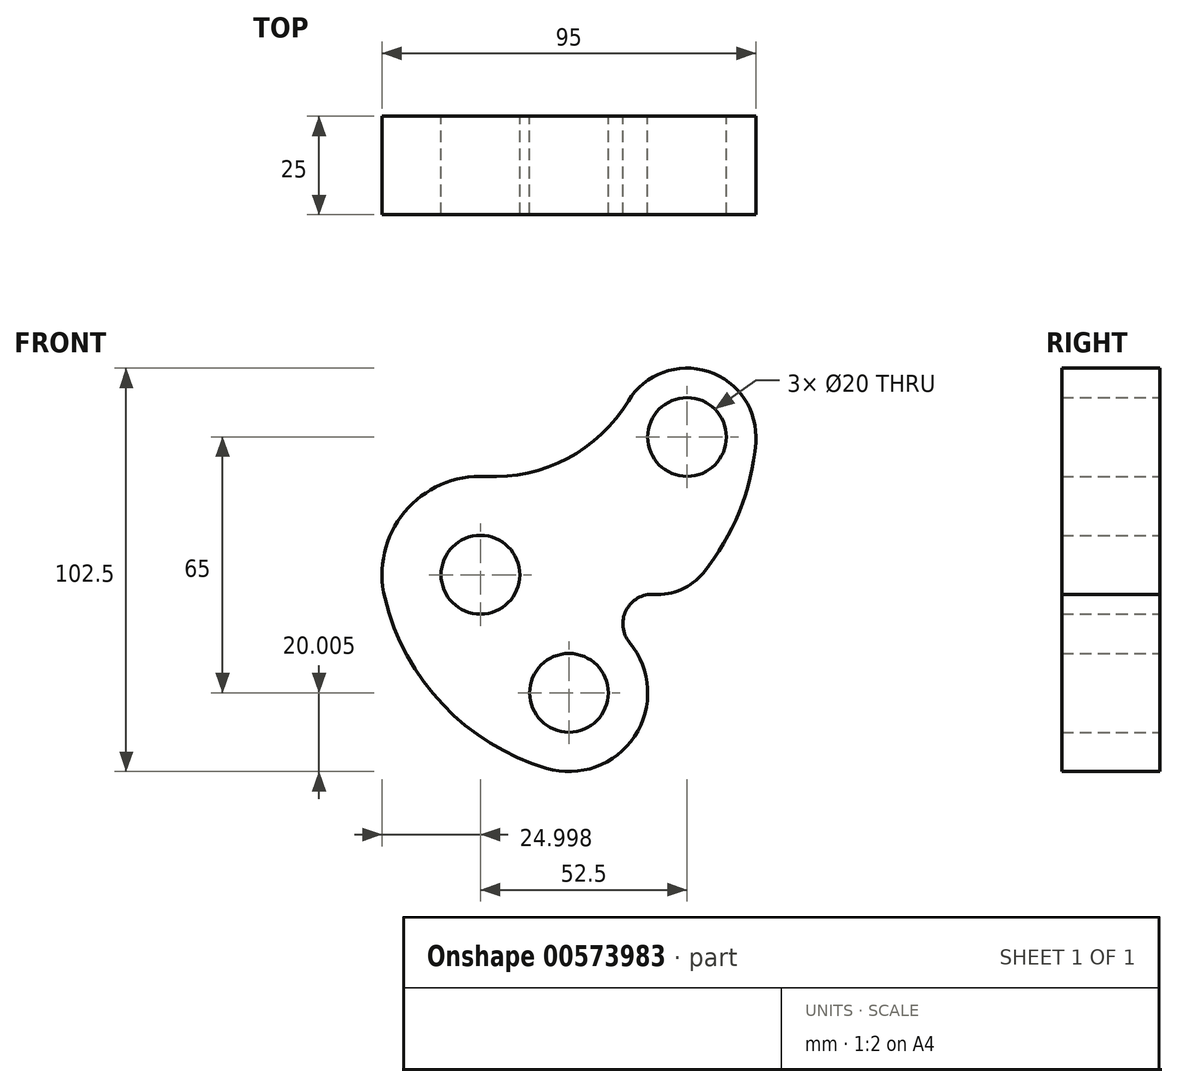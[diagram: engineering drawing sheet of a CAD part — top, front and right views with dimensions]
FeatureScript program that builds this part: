
annotation { "Feature Type Name" : "Feature", "Feature Type Description" : "" }
export const myFeature = defineFeature(function(context is Context, id is Id, definition is map)
    precondition{}
    {
        {
            var Q0;
            Q0=qCreatedBy(makeId("Front.planeOp"),FACE);
            var sketch = newSketch(context, id + "F0", { "sketchPlane" : qUnion([Q0])});
            skCircle(sketch, "E0", {"center": v(31.17, 52.24) * mm, "radius": 10 * mm});
            skCircle(sketch, "E1", {"center": v(-21.33, 17.24) * mm, "radius": 10 * mm});
            skCircle(sketch, "E2", {"center": v(1.17, -12.76) * mm, "radius": 10 * mm});
            skArc(sketch, "E3", {"start": v(-4.58, -31.91) * mm, "mid": v(17.84, -23.8) * mm, "end": v(16.57, 0) * mm});
            skArc(sketch, "E4", {"start": v(-20.03, 42.21) * mm, "mid": v(-40.59, 33.19) * mm, "end": v(-45.62, 11.3) * mm});
            skArc(sketch, "E5", {"start": v(48.6, 50.82) * mm, "mid": v(36.58, 68.89) * mm, "end": v(16.22, 61.35) * mm});
            skArc(sketch, "E6", {"start": v(-20.03, 42.21) * mm, "mid": v(0.73, 46.78) * mm, "end": v(16.22, 61.35) * mm});
            skArc(sketch, "E7", {"start": v(-45.62, 11.3) * mm, "mid": v(-30.84, -15.76) * mm, "end": v(-4.58, -31.91) * mm});
            skArc(sketch, "E8", {"start": v(22.79, 12.27) * mm, "mid": v(29.7, 13.51) * mm, "end": v(35.29, 17.76) * mm});
            skArc(sketch, "E9", {"start": v(35.29, 17.76) * mm, "mid": v(44.46, 33.28) * mm, "end": v(48.6, 50.82) * mm});
            skArc(sketch, "E10", {"start": v(22.79, 12.27) * mm, "mid": v(15.66, 8.17) * mm, "end": v(16.57, 0) * mm});
            skSolve(sketch);
        }
        {
            var Q0;
            Q0=makeQuery(id+"F0.imprint","IMPRINT",FACE,{"disambiguationData":[TD([[makeQuery(id+"F0.imprint","IMPRINT",EDGE,{"derivedFrom":sQuery(id+"F0.wireOp",EDGE,"E0")}),-1.0]])]});
            extrude(context, id + "F1", {"entities" : qUnion([Q0]), "depth" : 25 * mm, "offsetDistance" : 25 * mm});
        }
    });
